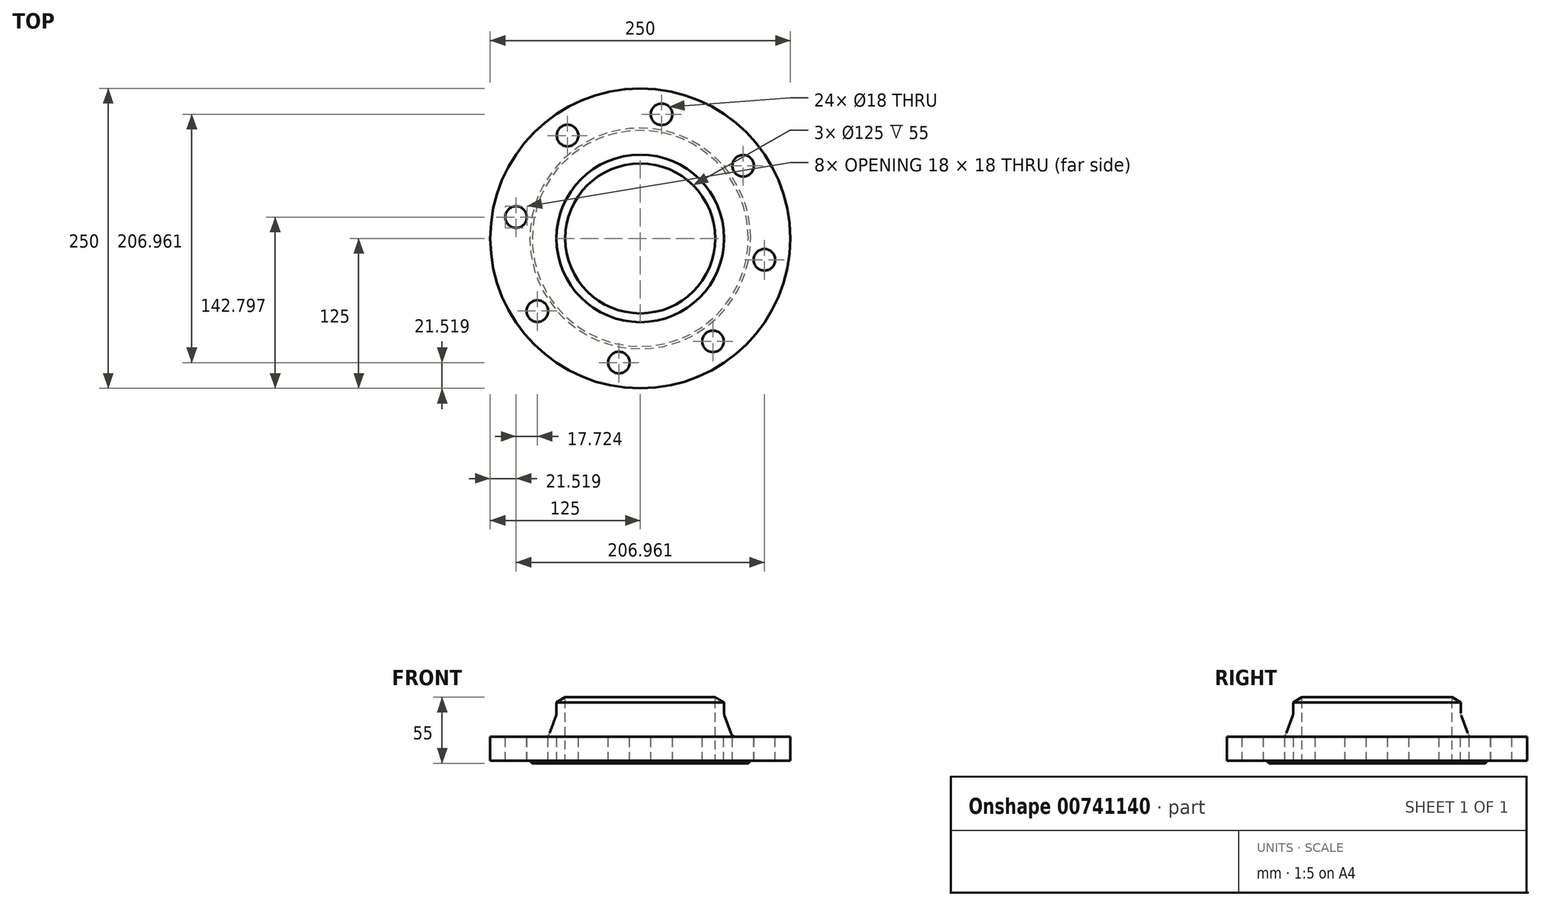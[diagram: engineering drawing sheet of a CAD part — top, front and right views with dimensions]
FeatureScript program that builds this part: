
annotation { "Feature Type Name" : "Feature", "Feature Type Description" : "" }
export const myFeature = defineFeature(function(context is Context, id is Id, definition is map)
    precondition{}
    {
        {
            var Q0;
            Q0=qCreatedBy(makeId("Front.planeOp"),FACE);
            var sketch = newSketch(context, id + "F0", { "sketchPlane" : qUnion([Q0])});
            skLineSegment(sketch, "E0", {"start": v(0, 94.05) * mm, "end": v(0, -88.04) * mm, "construction": true});
            skLineSegment(sketch, "E1", {"start": v(-62.5, 0) * mm, "end": v(-62.5, 53) * mm});
            skLineSegment(sketch, "E2", {"start": v(-62.5, 53) * mm, "end": v(-69.85, 48.76) * mm});
            skLineSegment(sketch, "E3", {"start": v(-76.68, 20) * mm, "end": v(-125, 20) * mm});
            skLineSegment(sketch, "E4", {"start": v(-125, 20) * mm, "end": v(-125, 0) * mm});
            skLineSegment(sketch, "E5", {"start": v(-125, 0) * mm, "end": v(-92, 0) * mm});
            skLineSegment(sketch, "E6", {"start": v(-69.85, 48.76) * mm, "end": v(-69.85, 38.76) * mm});
            skLineSegment(sketch, "E7", {"start": v(-69.85, 38.76) * mm, "end": v(-76.68, 20) * mm});
            skLineSegment(sketch, "E8", {"start": v(-92, 0) * mm, "end": v(-90, -2) * mm});
            skLineSegment(sketch, "E9", {"start": v(-90, -2) * mm, "end": v(-62.5, -2) * mm});
            skLineSegment(sketch, "E10", {"start": v(-62.5, -2) * mm, "end": v(-62.5, 0) * mm});
            skSolve(sketch);
        }
        {
            var Q0;
            Q0=makeQuery(id+"F0.imprint","IMPRINT",FACE,{"disambiguationData":[TD([[makeQuery(id+"F0.imprint","IMPRINT",EDGE,{"derivedFrom":sQuery(id+"F0.wireOp",EDGE,"E1")}),1.0]])]});
            var Q1;
            Q1=sQuery(id+"F0.wireOp",EDGE,"E0");
            revolve(context, id + "F1", {"surfaceOperationType" : NewSurfaceOperationType.NEW, "entities" : qUnion([Q0]), "axis" : qUnion([Q1]), "revolveType" : RevolveType.FULL});
        }
        {
            var Q0;
            Q0=makeQuery(id+"F1.opRevolve","SWEPT_FACE",FACE,{"disambiguationData":[OSD([sQuery(id+"F0.wireOp",EDGE,"E3")])]});
            var sketch = newSketch(context, id + "F2", { "sketchPlane" : qUnion([Q0])});
            skCircle(sketch, "E11", {"center": v(0, 0) * mm, "radius": 105 * mm, "construction": true});
            skCircle(sketch, "E12", {"center": v(-60.59, 85.76) * mm, "radius": 9 * mm});
            skCircle(sketch, "E13.1.0", {"center": v(-103.48, 17.8) * mm, "radius": 9 * mm});
            skCircle(sketch, "E13.2.0", {"center": v(-85.76, -60.59) * mm, "radius": 9 * mm});
            skCircle(sketch, "E13.3.0", {"center": v(-17.8, -103.48) * mm, "radius": 9 * mm});
            skCircle(sketch, "E13.4.0", {"center": v(60.59, -85.76) * mm, "radius": 9 * mm});
            skCircle(sketch, "E13.5.0", {"center": v(103.48, -17.8) * mm, "radius": 9 * mm});
            skCircle(sketch, "E13.6.0", {"center": v(85.76, 60.59) * mm, "radius": 9 * mm});
            skCircle(sketch, "E13.7.0", {"center": v(17.8, 103.48) * mm, "radius": 9 * mm});
            skSolve(sketch);
        }
        {
            var Q0;
            Q0 = qSketchRegion(id + "F2", true);
            extrude(context, id + "F3", {"entities" : qUnion([Q0]), "operationType" : NewBodyOperationType.REMOVE, "oppositeDirection" : true, "depth" : 25 * mm, "offsetDistance" : 25 * mm});
        }
        {
            var Q0;
            Q0=makeQuery(id+"F1.opRevolve","SWEPT_EDGE",EDGE,{"disambiguationData":[OSD([sQuery(id+"F0.wireOp",EDGE,"E3"),sQuery(id+"F0.wireOp",EDGE,"E7")])]});
            var Q1;
            Q1=makeQuery(id+"F1.opRevolve","SWEPT_EDGE",EDGE,{"disambiguationData":[OSD([sQuery(id+"F0.wireOp",EDGE,"E6"),sQuery(id+"F0.wireOp",EDGE,"E7")])]});
            fillet(context, id + "F4", {"entities" : qUnion([Q0, Q1]), "radius" : 5 * mm, "tangentPropagation" : true, "allowEdgeOverflow" : false});
        }
    });
